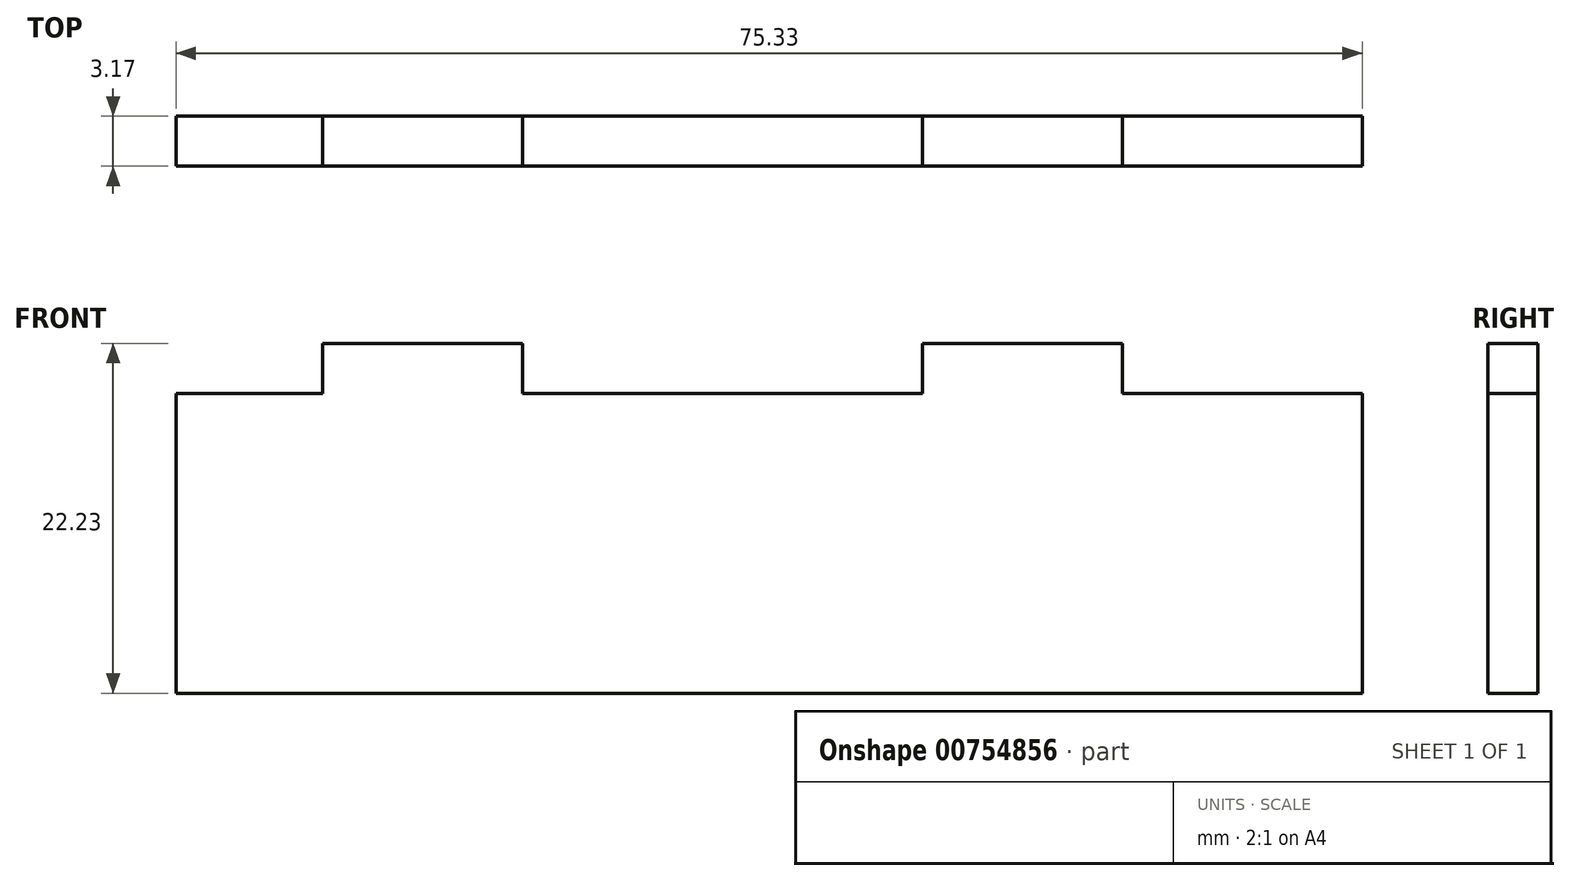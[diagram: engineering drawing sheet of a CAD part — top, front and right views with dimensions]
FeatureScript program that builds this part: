
annotation { "Feature Type Name" : "Feature", "Feature Type Description" : "" }
export const myFeature = defineFeature(function(context is Context, id is Id, definition is map)
    precondition{}
    {
        {
            var Q0;
            Q0=qCreatedBy(makeId("Front.planeOp"),FACE);
            var sketch = newSketch(context, id + "F0", { "sketchPlane" : qUnion([Q0])});
            skLineSegment(sketch, "E0.bottom", {"start": v(-34.69, 14.93) * mm, "end": v(-25.4, 14.93) * mm});
            skLineSegment(sketch, "E0.top", {"start": v(-34.69, -4.12) * mm, "end": v(40.64, -4.12) * mm});
            skLineSegment(sketch, "E0.left", {"start": v(-34.69, 14.93) * mm, "end": v(-34.69, -4.12) * mm});
            skLineSegment(sketch, "E0.right", {"start": v(40.64, 14.93) * mm, "end": v(40.64, -4.12) * mm});
            skLineSegment(sketch, "E1.top", {"start": v(-25.4, 18.1) * mm, "end": v(-12.7, 18.1) * mm});
            skLineSegment(sketch, "E1.left", {"start": v(-25.4, 14.93) * mm, "end": v(-25.4, 18.1) * mm});
            skLineSegment(sketch, "E1.right", {"start": v(-12.7, 14.93) * mm, "end": v(-12.7, 18.1) * mm});
            skLineSegment(sketch, "E2", {"start": v(0, -4.12) * mm, "end": v(0, 58.91) * mm});
            skLineSegment(sketch, "E3.MirrorCS", {"start": v(25.4, 18.1) * mm, "end": v(12.7, 18.1) * mm});
            skLineSegment(sketch, "E4.MirrorCS", {"start": v(12.7, 14.93) * mm, "end": v(12.7, 18.1) * mm});
            skLineSegment(sketch, "E5.MirrorCS", {"start": v(25.4, 14.93) * mm, "end": v(25.4, 18.1) * mm});
            skLineSegment(sketch, "E6.trimOffspring", {"start": v(25.4, 14.93) * mm, "end": v(40.64, 14.93) * mm});
            skLineSegment(sketch, "E7.trimOffspring", {"start": v(-12.7, 14.93) * mm, "end": v(12.7, 14.93) * mm});
            skSolve(sketch);
        }
        {
            var Q0;
            {var subQ5=sQuery(id+"F0.wireOp",EDGE,"E0.right");Q0=makeQuery(id+"F0.imprint","IMPRINT",FACE,{"disambiguationData":[TD([[makeQuery(id+"F0.imprint","IMPRINT",EDGE,{"derivedFrom":subQ5}),-1.0]])]});}
            var Q1;
            Q1=makeQuery(id+"F0.imprint","IMPRINT",FACE,{"disambiguationData":[TD([[makeQuery(id+"F0.imprint","IMPRINT",EDGE,{"derivedFrom":sQuery(id+"F0.wireOp",EDGE,"E0.bottom")}),-1.0]])]});
            extrude(context, id + "F1", {"entities" : qUnion([Q0, Q1]), "depth" : 3.17 * mm, "offsetDistance" : 25.4 * mm});
        }
    });
